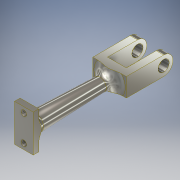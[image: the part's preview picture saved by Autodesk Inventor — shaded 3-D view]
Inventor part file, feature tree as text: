
AUTODESK INVENTOR PART (.ipt)
format: ipt  version: 2017 (Build 210142000, 142)  size: 244,736 bytes
history: native  units: mm
features: sketch x8, extrude x6, plane x3, fillet x3, loft x1
ambient origin geometry x8: Origin, YZ Plane, XZ Plane, XY Plane, X Axis, Y Axis, Z Axis, Center Point
bodies: Solid1 (feature_tree)
feature tree (21):
  sketch  "Sketch1"  dims[d0=9.5mm d1=43.0mm d2=6.5mm]
  plane  "Work Plane1"
  loft  "Loft1"
  extrude  "Extrusion1"  TaperAngle=0.0deg  [1 undecoded]
  extrude  "Extrusion2"  Depth=3.0mm TaperAngle=0.0deg
  extrude  "Extrusion3"  Depth=3.0mm
  fillet  "Fillet1"  [1 undecoded]
  extrude  "Extrusion5"  Depth=5.0mm
  fillet  "Fillet4"  Radius=5.0mm
  sketch  "Sketch10"  dims[d35=0.0mm d36=5.0mm d37=0.0mm]
  plane  "Work Plane3"
  plane  "Work Plane2"
  extrude  "Extrusion10"  Depth=5.0mm
  fillet  "Fillet6"  [1 undecoded]
  extrude  "Extrusion11"  TaperAngle=0.0deg  [1 undecoded]
  sketch  "Sketch2"  dims[d3=0.0mm d4=90.0deg d5=0.0mm d6=90.0deg]
  sketch  "Sketch3"  dims[d7=5.0mm d8=10.0mm d9=10.0mm d10=20.0mm d11=10.0mm d12=3.0mm d13=0.0mm]
  sketch  "Sketch4"  dims[d14=10.0mm d15=3.0mm d16=0.0mm]
  sketch  "Sketch5"  dims[d17=3.0mm d18=14.0mm d19=3.0mm d20=3.0mm d21=5.0mm d22=0.0mm d29=3.0mm d31=0.0mm]
  sketch  "Sketch7"  dims[d32=0.0mm d33=9.5mm d34=5.0mm]
  sketch  "Sketch12"  dims[d38=0.0mm d39=0.0mm d40=10.0mm d41=5.0mm d42=0.0mm d43=10.0mm d61=4.0mm d62=0.0mm d71=5.0mm d79=10.0mm d80=4.5mm d81=10.0mm d82=14.0mm d83=18.0mm d84=9.0mm d85=4.0mm d86=9.0mm d87=9.0mm d97=0.59mm d102=10.054mm d103=90.0deg d105=90.0deg d106=2.07063mm d108=18.0mm d109=18.0mm d110=21.0mm d111=0.0mm d112=5.0mm d113=6.0mm d114=21.0mm d115=0.0mm]
note: 4 required parameter values undecoded (feature->parameter linkage not recoverable at this tier; creation-order binding heuristic only, values carry confidence <= 0.55)
